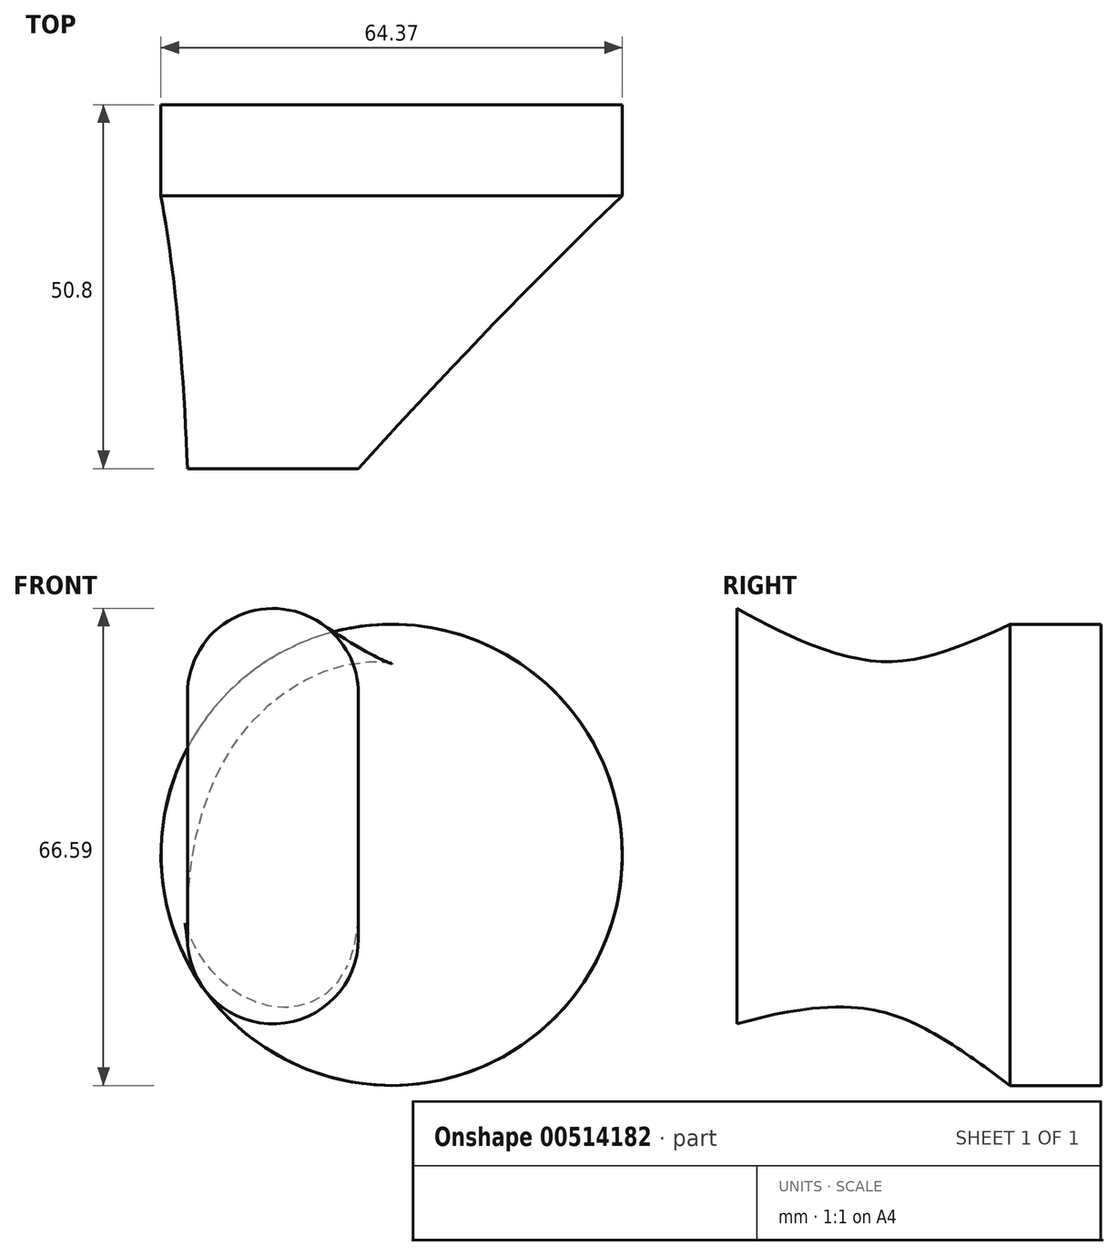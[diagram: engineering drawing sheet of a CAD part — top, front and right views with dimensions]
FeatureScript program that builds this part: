
annotation { "Feature Type Name" : "Feature", "Feature Type Description" : "" }
export const myFeature = defineFeature(function(context is Context, id is Id, definition is map)
    precondition{}
    {
        {
            var Q0;
            Q0=qCreatedBy(makeId("Front.planeOp"),FACE);
            var sketch = newSketch(context, id + "F0", { "sketchPlane" : qUnion([Q0])});
            skArc(sketch, "E0", {"start": v(10.75, 50.87) * mm, "mid": v(4.6, 31.16) * mm, "end": v(11.7, 11.77) * mm});
            skArc(sketch, "E1", {"start": v(63.95, 49.18) * mm, "mid": v(37.8, 64.1) * mm, "end": v(10.75, 50.87) * mm});
            skArc(sketch, "E2", {"start": v(11.7, 11.77) * mm, "mid": v(35.33, -0.21) * mm, "end": v(59.95, 9.6) * mm});
            skArc(sketch, "E3", {"start": v(59.95, 9.6) * mm, "mid": v(68.8, 28.7) * mm, "end": v(63.95, 49.18) * mm});
            skSolve(sketch);
        }
        {
            var Q0;
            Q0=qCreatedBy(makeId("Front.planeOp"),FACE);
            cPlane(context, id + "F1", {"entities" : qUnion([Q0]), "cplaneType" : CPlaneType.OFFSET, "offset" : 50.8 * mm, "width" : 152.4 * mm, "height" : 152.4 * mm});
        }
        {
            var Q0;
            Q0=qCreatedBy(id+"F1.planeOp",FACE);
            var sketch = newSketch(context, id + "F2", { "sketchPlane" : qUnion([Q0])});
            skLineSegment(sketch, "E4.bottom", {"start": v(32.14, 20.27) * mm, "end": v(8.3, 20.27) * mm, "construction": true});
            skLineSegment(sketch, "E4.top", {"start": v(32.14, 54.41) * mm, "end": v(8.3, 54.41) * mm, "construction": true});
            skLineSegment(sketch, "E4.left", {"start": v(32.14, 20.27) * mm, "end": v(32.14, 54.41) * mm});
            skLineSegment(sketch, "E4.right", {"start": v(8.3, 20.27) * mm, "end": v(8.3, 54.41) * mm});
            skPoint(sketch, "E4.middle", {"position": v(20.21, 37.34) * mm});
            skArc(sketch, "E5", {"start": v(32.14, 54.41) * mm, "mid": v(20.21, 66.34) * mm, "end": v(8.3, 54.41) * mm});
            skArc(sketch, "E6", {"start": v(8.3, 20.27) * mm, "mid": v(20.21, 8.35) * mm, "end": v(32.14, 20.27) * mm});
            skSolve(sketch);
        }
        {
            var Q0;
            Q0=makeQuery(id+"F0.imprint","IMPRINT",FACE,{"disambiguationData":[TD([[makeQuery(id+"F0.imprint","IMPRINT",EDGE,{"derivedFrom":sQuery(id+"F0.wireOp",EDGE,"E0")}),1.0]])]});
            extrude(context, id + "F3", {"entities" : qUnion([Q0]), "depth" : 12.7 * mm, "offsetDistance" : 25.4 * mm});
        }
        {
            var Q0;
            Q0=makeQuery(id+"F3.opExtrude","CAP_FACE",FACE,{"disambiguationData":[OSD([sQuery(id+"F0.wireOp",EDGE,"E0"),sQuery(id+"F0.wireOp",EDGE,"E1"),sQuery(id+"F0.wireOp",EDGE,"E2"),sQuery(id+"F0.wireOp",EDGE,"E3")])],"isStart":false});
            var sketch = newSketch(context, id + "F4", { "sketchPlane" : qUnion([Q0])});
            skCircle(sketch, "E7.0", {"center": v(36.78, 31.94) * mm, "radius": 32.18 * mm});
            skPoint(sketch, "E8", {"position": v(62.2, 51.68) * mm});
            skPoint(sketch, "E9", {"position": v(58.01, 7.75) * mm});
            skPoint(sketch, "E10", {"position": v(20.24, 4.33) * mm});
            skPoint(sketch, "E11", {"position": v(13.08, 53.72) * mm});
            skSolve(sketch);
        }
        {
            var Q0;
            Q0=makeQuery(id+"F4.imprint","IMPRINT",FACE,{"disambiguationData":[TD([[makeQuery(id+"F4.imprint","IMPRINT",EDGE,{"derivedFrom":sQuery(id+"F4.wireOp",EDGE,"E7.0")}),1.0]])]});
            var Q1;
            Q1=makeQuery(id+"F2.imprint","IMPRINT",FACE,{"disambiguationData":[TD([[makeQuery(id+"F2.imprint","IMPRINT",EDGE,{"derivedFrom":sQuery(id+"F2.wireOp",EDGE,"E4.left")}),1.0]])]});
            var Q2;
            Q2=sQuery(id+"F2.wireOp",VERTEX,"E4.left.start");
            var Q3;
            Q3=sQuery(id+"F4.wireOp",VERTEX,"E9");
            var Q4;
            Q4=sQuery(id+"F2.wireOp",VERTEX,"E4.right.start");
            var Q5;
            Q5=sQuery(id+"F4.wireOp",VERTEX,"E10");
            loft(context, id + "F5", {"sheetProfilesArray" : [{ "sheetProfileEntities" : qUnion([Q0]) }, { "sheetProfileEntities" : qUnion([Q1]) }], "connections" : [{ "connectionEntities" : qUnion([Q2, Q3, Q4, Q5]), "connectionEdgeQueries" : qUnion([]), "connectionEdgeParameters" : [] }]});
        }
    });
